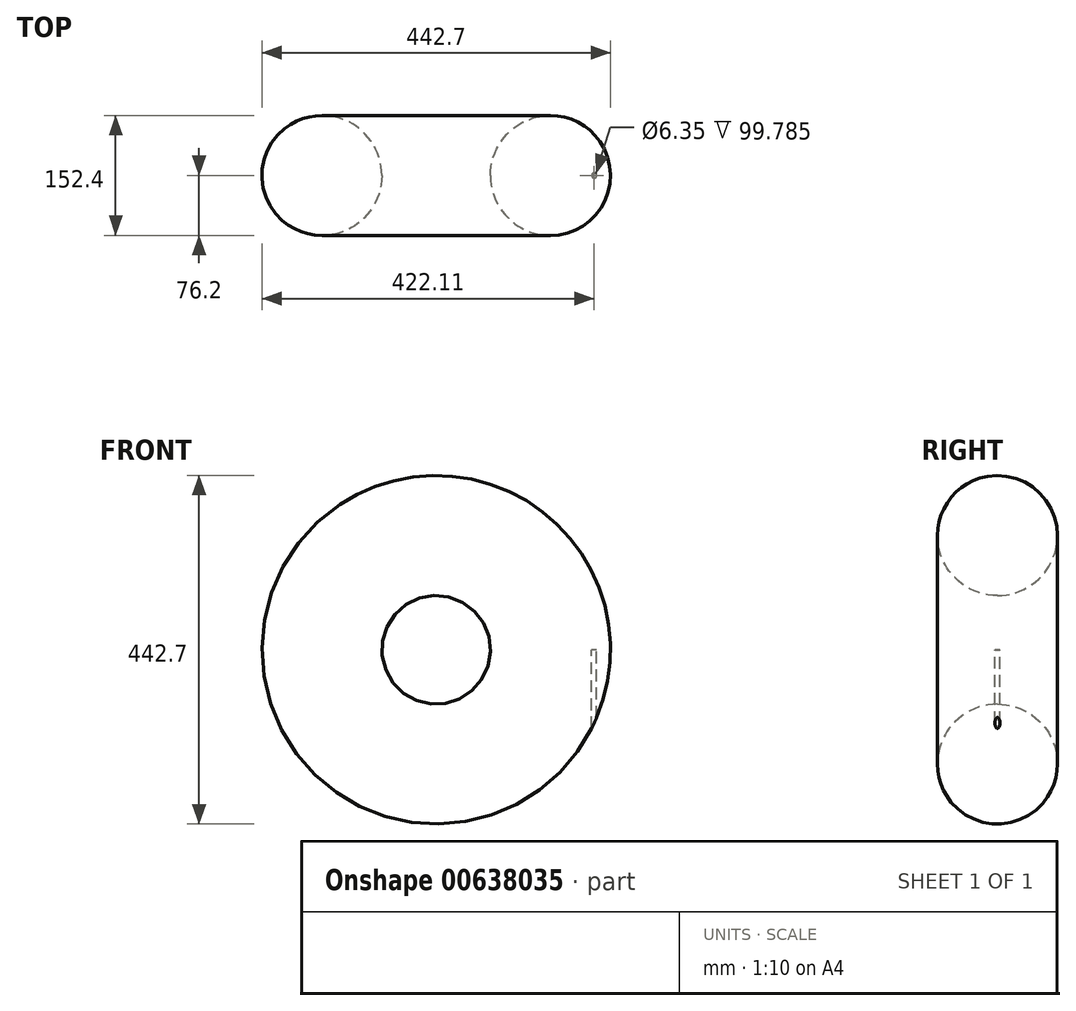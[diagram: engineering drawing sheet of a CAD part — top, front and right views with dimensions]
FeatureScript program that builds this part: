
annotation { "Feature Type Name" : "Feature", "Feature Type Description" : "" }
export const myFeature = defineFeature(function(context is Context, id is Id, definition is map)
    precondition{}
    {
        {
            var Q0;
            Q0=qCreatedBy(makeId("Top.planeOp"),FACE);
            var sketch = newSketch(context, id + "F0", { "sketchPlane" : qUnion([Q0])});
            skCircle(sketch, "E0", {"center": v(0, 0) * mm, "radius": 76.2 * mm});
            skLineSegment(sketch, "E1", {"start": v(-145.15, 0) * mm, "end": v(-145.15, 50.8) * mm, "construction": true});
            skSolve(sketch);
        }
        {
            var Q0;
            Q0 = qSketchRegion(id + "F0", true);
            var Q1;
            Q1=sQuery(id+"F0.wireOp",EDGE,"E1");
            revolve(context, id + "F1", {"entities" : qUnion([Q0]), "axis" : qUnion([Q1]), "revolveType" : RevolveType.FULL});
        }
        {
            var Q0;
            Q0=qCreatedBy(makeId("Top.planeOp"),FACE);
            var sketch = newSketch(context, id + "F2", { "sketchPlane" : qUnion([Q0])});
            skPoint(sketch, "E2", {"position": v(55.6, 0) * mm});
            skSolve(sketch);
        }
        {
            var Q0;
            Q0=sQuery(id+"F2.wireOp",VERTEX,"E2");
            var Q1;
            Q1=makeQuery(id+"F1.opRevolve","SWEPT_BODY",BODY,{"disambiguationData":[OSD([sQuery(id+"F0.wireOp",EDGE,"E0")])]});
            hole(context, id + "F3", {"style" : HoleStyle.SIMPLE, "endStyle" : HoleEndStyle.THROUGH, "holeDiameter" : 6.35 * mm, "majorDiameter" : 6.35 * mm, "isTappedThrough" : true, "tappedDepth" : 12.7 * mm, "tapClearance" : 3, "locations" : qUnion([Q0]), "scope" : qUnion([Q1])});
        }
    });
